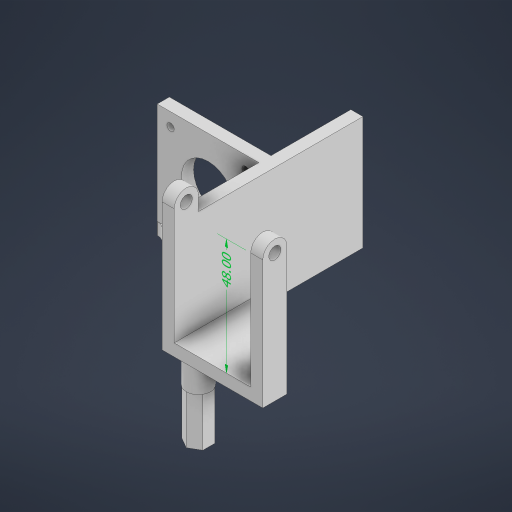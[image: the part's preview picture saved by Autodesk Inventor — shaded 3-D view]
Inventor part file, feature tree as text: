
AUTODESK INVENTOR PART (.ipt)
format: ipt  version: 2024.1 (Build 281209000, 209)  size: 605,696 bytes
history: native  units: mm
features: extrude x9, sketch x9, other x4, chamfer x2, fillet x1
ambient origin geometry x8: Origin, YZ Plane, XZ Plane, XY Plane, X Axis, Y Axis, Z Axis, Center Point
bodies: Body1 (feature_tree)
feature tree (25):
  other  "솔리드1"
  extrude  "돌출1"  Depth=5.0mm
  extrude  "돌출2"  Depth=10.0mm
  extrude  "돌출3"  Depth=53.0mm
  extrude  "돌출4"  Depth=10.0mm
  extrude  "돌출5"  Depth=5.0mm TaperAngle=0.0deg
  chamfer  "모따기1"  Distance=10.0mm
  extrude  "돌출6"  Depth=5.0mm
  extrude  "돌출7"  Depth=31.6mm TaperAngle=0.0deg
  extrude  "돌출8"  Depth=10.0mm
  other  "직접 편집1"
  fillet  "모깎기1"  Radius=53.0mm
  extrude  "돌출9"  Depth=5.0mm
  chamfer  "모따기2"  Distance=5.0mm
  sketch  "스케치1"
  sketch  "스케치2"
  sketch  "스케치3"
  sketch  "스케치4"
  sketch  "스케치5"
  sketch  "스케치6"
  sketch  "스케치7"
  sketch  "스케치8"
  sketch  "스케치9"
  other  "이동1"
  other  "선형 치수 1"
